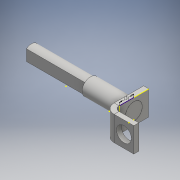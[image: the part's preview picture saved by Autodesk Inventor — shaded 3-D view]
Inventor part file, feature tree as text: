
AUTODESK INVENTOR PART (.ipt)
format: ipt  version: 2016 (Build 200138000, 138)  size: 180,736 bytes
history: native  units: mm
features: sketch x12, other x10, extrude x4
ambient origin geometry x8: Origin, YZ Plane, XZ Plane, XY Plane, X Axis, Y Axis, Z Axis, Center Point
bodies: Body1 (feature_tree)
feature tree (26):
  other  "Bryła1"
  other  "Powierzchnia1"
  sketch  "Szkic2"
  sketch  "Szkic3"
  other  "Kołnierz1"
  sketch  "Szkic5"
  sketch  "Szkic6"
  extrude  "Wyciągnięcie proste1"  Depth=5.0mm
  sketch  "Szkic7"
  other  "Powierzchnia2"
  extrude  "Wyciągnięcie proste2"  Depth=5.0mm
  extrude  "Wyciągnięcie proste3"  Depth=5.0mm
  sketch  "Szkic11"
  sketch  "Szkic12"
  extrude  "Wyciągnięcie proste4"  Depth=1.0mm
  sketch  "Szkic1"
  other  "Płyta1"
  sketch  "Szkic4"
  other  "Płyta2"
  other  "Gięcie1"
  other  "Narożnik1"
  sketch  "Szkic8"
  other  "Płyta3"
  other  "Gięcie2"
  sketch  "Szkic9"
  sketch  "Szkic10"
